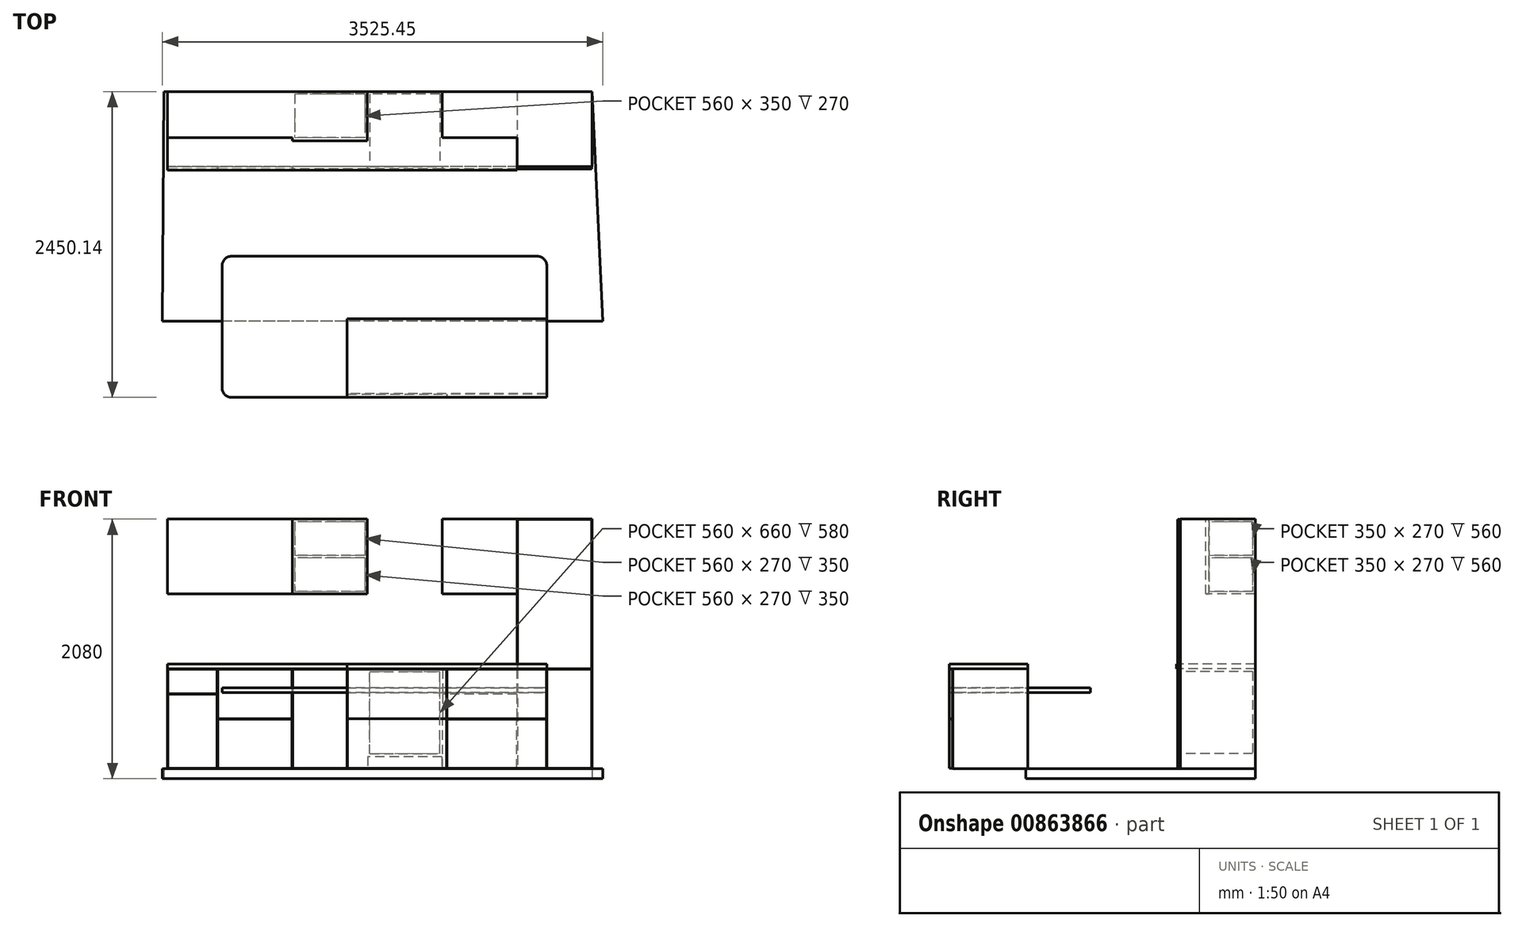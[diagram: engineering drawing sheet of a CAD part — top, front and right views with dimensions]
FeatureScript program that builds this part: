
annotation { "Feature Type Name" : "Feature", "Feature Type Description" : "" }
export const myFeature = defineFeature(function(context is Context, id is Id, definition is map)
    precondition{}
    {
        {
            var Q0;
            Q0=qCreatedBy(makeId("Top.planeOp"),FACE);
            var sketch = newSketch(context, id + "F0", { "sketchPlane" : qUnion([Q0])});
            skLineSegment(sketch, "E0", {"start": v(1715.97, -225.48) * mm, "end": v(-1714.03, -225.48) * mm});
            skLineSegment(sketch, "E1", {"start": v(1800.72, -2063.55) * mm, "end": v(1715.97, -225.48) * mm});
            skLineSegment(sketch, "E2", {"start": v(1800.72, -2063.55) * mm, "end": v(-1724.73, -2063.55) * mm});
            skLineSegment(sketch, "E3", {"start": v(-1714.03, -225.48) * mm, "end": v(-1724.73, -2063.55) * mm});
            skSolve(sketch);
        }
        {
            var Q0;
            Q0=makeQuery(id+"F0.imprint","IMPRINT",FACE,{"disambiguationData":[TD([[makeQuery(id+"F0.imprint","IMPRINT",EDGE,{"derivedFrom":sQuery(id+"F0.wireOp",EDGE,"E0")}),1.0]])]});
            var sketch = newSketch(context, id + "F1", { "sketchPlane" : qUnion([Q0])});
            skLineSegment(sketch, "E4.bottom", {"start": v(1715.97, -225.48) * mm, "end": v(1115.97, -225.48) * mm});
            skLineSegment(sketch, "E4.top", {"start": v(1715.97, -795.48) * mm, "end": v(1115.97, -795.48) * mm});
            skLineSegment(sketch, "E4.left", {"start": v(1715.97, -225.48) * mm, "end": v(1715.97, -795.48) * mm});
            skLineSegment(sketch, "E4.right", {"start": v(1115.97, -225.48) * mm, "end": v(1115.97, -795.48) * mm});
            skSolve(sketch);
        }
        {
            var Q0;
            Q0=makeQuery(id+"F1.imprint","IMPRINT",FACE,{"disambiguationData":[TD([[makeQuery(id+"F1.imprint","IMPRINT",EDGE,{"derivedFrom":sQuery(id+"F1.wireOp",EDGE,"E4.top")}),1.0]])]});
            var sketch = newSketch(context, id + "F2", { "sketchPlane" : qUnion([Q0])});
            skLineSegment(sketch, "E5.bottom", {"start": v(1115.97, -225.48) * mm, "end": v(515.97, -225.48) * mm});
            skLineSegment(sketch, "E5.top", {"start": v(1115.97, -795.48) * mm, "end": v(515.97, -795.48) * mm});
            skLineSegment(sketch, "E5.left", {"start": v(1115.97, -225.48) * mm, "end": v(1115.97, -795.48) * mm});
            skLineSegment(sketch, "E5.right", {"start": v(515.97, -225.48) * mm, "end": v(515.97, -795.48) * mm});
            skSolve(sketch);
        }
        {
            var Q0;
            Q0=makeQuery(id+"F1.imprint","IMPRINT",FACE,{"disambiguationData":[TD([[makeQuery(id+"F1.imprint","IMPRINT",EDGE,{"derivedFrom":sQuery(id+"F1.wireOp",EDGE,"E4.top")}),1.0]])]});
            var sketch = newSketch(context, id + "F3", { "sketchPlane" : qUnion([Q0])});
            skLineSegment(sketch, "E6.bottom", {"start": v(515.97, -225.48) * mm, "end": v(-84.03, -225.48) * mm});
            skLineSegment(sketch, "E6.top", {"start": v(515.97, -795.48) * mm, "end": v(-84.03, -795.48) * mm});
            skLineSegment(sketch, "E6.left", {"start": v(515.97, -225.48) * mm, "end": v(515.97, -795.48) * mm});
            skLineSegment(sketch, "E6.right", {"start": v(-84.03, -225.48) * mm, "end": v(-84.03, -795.48) * mm});
            skSolve(sketch);
        }
        {
            var Q0;
            Q0=makeQuery(id+"F3.imprint","IMPRINT",FACE,{"disambiguationData":[TD([[makeQuery(id+"F3.imprint","IMPRINT",EDGE,{"derivedFrom":sQuery(id+"F3.wireOp",EDGE,"E6.top")}),1.0]])]});
            var sketch = newSketch(context, id + "F4", { "sketchPlane" : qUnion([Q0])});
            skLineSegment(sketch, "E7.bottom", {"start": v(-84.03, -225.48) * mm, "end": v(-684.03, -225.48) * mm});
            skLineSegment(sketch, "E7.top", {"start": v(-84.03, -795.48) * mm, "end": v(-684.03, -795.48) * mm});
            skLineSegment(sketch, "E7.left", {"start": v(-84.03, -225.48) * mm, "end": v(-84.03, -795.48) * mm});
            skLineSegment(sketch, "E7.right", {"start": v(-684.03, -225.48) * mm, "end": v(-684.03, -795.48) * mm});
            skSolve(sketch);
        }
        {
            var Q0;
            Q0=makeQuery(id+"F4.imprint","IMPRINT",FACE,{"disambiguationData":[TD([[makeQuery(id+"F4.imprint","IMPRINT",EDGE,{"derivedFrom":sQuery(id+"F4.wireOp",EDGE,"E7.top")}),1.0]])]});
            var sketch = newSketch(context, id + "F5", { "sketchPlane" : qUnion([Q0])});
            skLineSegment(sketch, "E8.bottom", {"start": v(-684.03, -225.48) * mm, "end": v(-1284.03, -225.48) * mm});
            skLineSegment(sketch, "E8.top", {"start": v(-684.03, -795.48) * mm, "end": v(-1284.03, -795.48) * mm});
            skLineSegment(sketch, "E8.left", {"start": v(-684.03, -225.48) * mm, "end": v(-684.03, -795.48) * mm});
            skLineSegment(sketch, "E8.right", {"start": v(-1284.03, -225.48) * mm, "end": v(-1284.03, -795.48) * mm});
            skSolve(sketch);
        }
        {
            var Q0;
            Q0=makeQuery(id+"F1.imprint","IMPRINT",FACE,{"disambiguationData":[TD([[makeQuery(id+"F1.imprint","IMPRINT",EDGE,{"derivedFrom":sQuery(id+"F1.wireOp",EDGE,"E4.bottom")}),1.0]])]});
            cPlane(context, id + "F6", {"entities" : qUnion([Q0]), "cplaneType" : CPlaneType.OFFSET, "offset" : 80 * mm, "width" : 150 * mm, "height" : 150 * mm});
        }
        {
            var Q0;
            Q0=qCreatedBy(id+"F6.planeOp",FACE);
            var sketch = newSketch(context, id + "F7", { "sketchPlane" : qUnion([Q0])});
            skLineSegment(sketch, "E9.bottom", {"start": v(1715.97, -225.48) * mm, "end": v(1115.97, -225.48) * mm});
            skLineSegment(sketch, "E9.top", {"start": v(1715.97, -825.48) * mm, "end": v(1115.97, -825.48) * mm});
            skLineSegment(sketch, "E9.left", {"start": v(1715.97, -225.48) * mm, "end": v(1715.97, -825.48) * mm});
            skLineSegment(sketch, "E9.right", {"start": v(1115.97, -225.48) * mm, "end": v(1115.97, -825.48) * mm});
            skSolve(sketch);
        }
        {
            var Q0;
            Q0=qCreatedBy(id+"F6.planeOp",FACE);
            var sketch = newSketch(context, id + "F8", { "sketchPlane" : qUnion([Q0])});
            skLineSegment(sketch, "E10.bottom", {"start": v(1115.97, -225.48) * mm, "end": v(515.97, -225.48) * mm});
            skLineSegment(sketch, "E10.top", {"start": v(1115.97, -825.48) * mm, "end": v(515.97, -825.48) * mm});
            skLineSegment(sketch, "E10.left", {"start": v(1115.97, -225.48) * mm, "end": v(1115.97, -825.48) * mm});
            skLineSegment(sketch, "E10.right", {"start": v(515.97, -225.48) * mm, "end": v(515.97, -825.48) * mm});
            skSolve(sketch);
        }
        {
            var Q0;
            Q0=qCreatedBy(id+"F6.planeOp",FACE);
            var sketch = newSketch(context, id + "F9", { "sketchPlane" : qUnion([Q0])});
            skLineSegment(sketch, "E11.bottom", {"start": v(515.97, -225.48) * mm, "end": v(-84.03, -225.48) * mm});
            skLineSegment(sketch, "E11.top", {"start": v(515.97, -825.48) * mm, "end": v(-84.03, -825.48) * mm});
            skLineSegment(sketch, "E11.left", {"start": v(515.97, -225.48) * mm, "end": v(515.97, -825.48) * mm});
            skLineSegment(sketch, "E11.right", {"start": v(-84.03, -225.48) * mm, "end": v(-84.03, -825.48) * mm});
            skSolve(sketch);
        }
        {
            var Q0;
            Q0=qCreatedBy(id+"F6.planeOp",FACE);
            var sketch = newSketch(context, id + "F10", { "sketchPlane" : qUnion([Q0])});
            skLineSegment(sketch, "E12.bottom", {"start": v(-84.03, -225.48) * mm, "end": v(-684.03, -225.48) * mm});
            skLineSegment(sketch, "E12.top", {"start": v(-84.03, -825.48) * mm, "end": v(-684.03, -825.48) * mm});
            skLineSegment(sketch, "E12.left", {"start": v(-84.03, -225.48) * mm, "end": v(-84.03, -825.48) * mm});
            skLineSegment(sketch, "E12.right", {"start": v(-684.03, -225.48) * mm, "end": v(-684.03, -825.48) * mm});
            skSolve(sketch);
        }
        {
            var Q0;
            Q0=qCreatedBy(id+"F6.planeOp",FACE);
            var sketch = newSketch(context, id + "F11", { "sketchPlane" : qUnion([Q0])});
            skLineSegment(sketch, "E13.bottom", {"start": v(-684.03, -225.48) * mm, "end": v(-1284.03, -225.48) * mm});
            skLineSegment(sketch, "E13.top", {"start": v(-684.03, -825.48) * mm, "end": v(-1284.03, -825.48) * mm});
            skLineSegment(sketch, "E13.left", {"start": v(-684.03, -225.48) * mm, "end": v(-684.03, -825.48) * mm});
            skLineSegment(sketch, "E13.right", {"start": v(-1284.03, -225.48) * mm, "end": v(-1284.03, -825.48) * mm});
            skSolve(sketch);
        }
        {
            var Q0;
            Q0=qCreatedBy(id+"F6.planeOp",FACE);
            var sketch = newSketch(context, id + "F12", { "sketchPlane" : qUnion([Q0])});
            skLineSegment(sketch, "E14.bottom", {"start": v(-1284.03, -225.48) * mm, "end": v(-1684.03, -225.48) * mm});
            skLineSegment(sketch, "E14.top", {"start": v(-1284.03, -825.48) * mm, "end": v(-1684.03, -825.48) * mm});
            skLineSegment(sketch, "E14.left", {"start": v(-1284.03, -225.48) * mm, "end": v(-1284.03, -825.48) * mm});
            skLineSegment(sketch, "E14.right", {"start": v(-1684.03, -225.48) * mm, "end": v(-1684.03, -825.48) * mm});
            skSolve(sketch);
        }
        {
            var Q0;
            Q0=makeQuery(id+"F7.imprint","IMPRINT",FACE,{"disambiguationData":[TD([[makeQuery(id+"F7.imprint","IMPRINT",EDGE,{"derivedFrom":sQuery(id+"F7.wireOp",EDGE,"E9.bottom")}),1.0]])]});
            extrude(context, id + "F13", {"entities" : qUnion([Q0]), "depth" : 2000 * mm, "offsetDistance" : 25 * mm});
        }
        {
            var Q0;
            Q0=makeQuery(id+"F8.imprint","IMPRINT",FACE,{"disambiguationData":[TD([[makeQuery(id+"F8.imprint","IMPRINT",EDGE,{"derivedFrom":sQuery(id+"F8.wireOp",EDGE,"E10.bottom")}),1.0]])]});
            extrude(context, id + "F14", {"entities" : qUnion([Q0]), "operationType" : NewBodyOperationType.ADD, "depth" : 800 * mm, "offsetDistance" : 25 * mm});
        }
        {
            var Q0;
            Q0=makeQuery(id+"F9.imprint","IMPRINT",FACE,{"disambiguationData":[TD([[makeQuery(id+"F9.imprint","IMPRINT",EDGE,{"derivedFrom":sQuery(id+"F9.wireOp",EDGE,"E11.bottom")}),1.0]])]});
            extrude(context, id + "F15", {"entities" : qUnion([Q0]), "operationType" : NewBodyOperationType.ADD, "depth" : 800 * mm, "offsetDistance" : 25 * mm});
        }
        {
            var Q0;
            Q0=makeQuery(id+"F10.imprint","IMPRINT",FACE,{"disambiguationData":[TD([[makeQuery(id+"F10.imprint","IMPRINT",EDGE,{"derivedFrom":sQuery(id+"F10.wireOp",EDGE,"E12.bottom")}),1.0]])]});
            extrude(context, id + "F16", {"entities" : qUnion([Q0]), "operationType" : NewBodyOperationType.ADD, "depth" : 800 * mm, "offsetDistance" : 25 * mm});
        }
        {
            var Q0;
            Q0=makeQuery(id+"F11.imprint","IMPRINT",FACE,{"disambiguationData":[TD([[makeQuery(id+"F11.imprint","IMPRINT",EDGE,{"derivedFrom":sQuery(id+"F11.wireOp",EDGE,"E13.bottom")}),1.0]])]});
            extrude(context, id + "F17", {"entities" : qUnion([Q0]), "operationType" : NewBodyOperationType.ADD, "depth" : 800 * mm, "offsetDistance" : 25 * mm});
        }
        {
            var Q0;
            Q0=makeQuery(id+"F12.imprint","IMPRINT",FACE,{"disambiguationData":[TD([[makeQuery(id+"F12.imprint","IMPRINT",EDGE,{"derivedFrom":sQuery(id+"F12.wireOp",EDGE,"E14.bottom")}),1.0]])]});
            extrude(context, id + "F18", {"entities" : qUnion([Q0]), "operationType" : NewBodyOperationType.ADD, "depth" : 800 * mm, "offsetDistance" : 25 * mm});
        }
        {
            var Q0;
            Q0=makeQuery(id+"F13.opExtrude","CAP_FACE",FACE,{"disambiguationData":[OSD([sQuery(id+"F7.wireOp",EDGE,"E9.bottom"),sQuery(id+"F7.wireOp",EDGE,"E9.top"),sQuery(id+"F7.wireOp",EDGE,"E9.left"),sQuery(id+"F7.wireOp",EDGE,"E9.right")])],"isStart":false});
            var sketch = newSketch(context, id + "F19", { "sketchPlane" : qUnion([Q0])});
            skLineSegment(sketch, "E15.bottom", {"start": v(1115.97, -225.48) * mm, "end": v(515.97, -225.48) * mm});
            skLineSegment(sketch, "E15.top", {"start": v(1115.97, -595.48) * mm, "end": v(515.97, -595.48) * mm});
            skLineSegment(sketch, "E15.left", {"start": v(1115.97, -225.48) * mm, "end": v(1115.97, -595.48) * mm});
            skLineSegment(sketch, "E15.right", {"start": v(515.97, -225.48) * mm, "end": v(515.97, -595.48) * mm});
            skSolve(sketch);
        }
        {
            var Q0;
            Q0=makeQuery(id+"F19.imprint","IMPRINT",FACE,{"disambiguationData":[TD([[makeQuery(id+"F19.imprint","IMPRINT",EDGE,{"derivedFrom":sQuery(id+"F19.wireOp",EDGE,"E15.bottom")}),1.0]])]});
            var sketch = newSketch(context, id + "F20", { "sketchPlane" : qUnion([Q0])});
            skLineSegment(sketch, "E16.bottom", {"start": v(515.97, -225.48) * mm, "end": v(-84.03, -225.48) * mm});
            skLineSegment(sketch, "E16.top", {"start": v(515.97, -595.48) * mm, "end": v(-84.03, -595.48) * mm});
            skLineSegment(sketch, "E16.left", {"start": v(515.97, -225.48) * mm, "end": v(515.97, -595.48) * mm});
            skLineSegment(sketch, "E16.right", {"start": v(-84.03, -225.48) * mm, "end": v(-84.03, -595.48) * mm});
            skSolve(sketch);
        }
        {
            var Q0;
            Q0=makeQuery(id+"F20.imprint","IMPRINT",FACE,{"disambiguationData":[TD([[makeQuery(id+"F20.imprint","IMPRINT",EDGE,{"derivedFrom":sQuery(id+"F20.wireOp",EDGE,"E16.bottom")}),1.0]])]});
            var sketch = newSketch(context, id + "F21", { "sketchPlane" : qUnion([Q0])});
            skLineSegment(sketch, "E17.bottom", {"start": v(-84.03, -225.48) * mm, "end": v(-684.03, -225.48) * mm});
            skLineSegment(sketch, "E17.top", {"start": v(-84.03, -595.48) * mm, "end": v(-684.03, -595.48) * mm});
            skLineSegment(sketch, "E17.left", {"start": v(-84.03, -225.48) * mm, "end": v(-84.03, -595.48) * mm});
            skLineSegment(sketch, "E17.right", {"start": v(-684.03, -225.48) * mm, "end": v(-684.03, -595.48) * mm});
            skSolve(sketch);
        }
        {
            var Q0;
            Q0=makeQuery(id+"F21.imprint","IMPRINT",FACE,{"disambiguationData":[TD([[makeQuery(id+"F21.imprint","IMPRINT",EDGE,{"derivedFrom":sQuery(id+"F21.wireOp",EDGE,"E17.bottom")}),1.0]])]});
            var sketch = newSketch(context, id + "F22", { "sketchPlane" : qUnion([Q0])});
            skLineSegment(sketch, "E18.bottom", {"start": v(-684.03, -225.48) * mm, "end": v(-1284.03, -225.48) * mm});
            skLineSegment(sketch, "E18.top", {"start": v(-684.03, -595.48) * mm, "end": v(-1284.03, -595.48) * mm});
            skLineSegment(sketch, "E18.left", {"start": v(-684.03, -225.48) * mm, "end": v(-684.03, -595.48) * mm});
            skLineSegment(sketch, "E18.right", {"start": v(-1284.03, -225.48) * mm, "end": v(-1284.03, -595.48) * mm});
            skSolve(sketch);
        }
        {
            var Q0;
            Q0=makeQuery(id+"F18.boolean.opBoolean","MERGE",FACE,{"derivedFrom":[makeQuery(id+"F17.boolean.opBoolean","MERGE",FACE,{"derivedFrom":[makeQuery(id+"F16.boolean.opBoolean","MERGE",FACE,{"derivedFrom":[makeQuery(id+"F15.boolean.opBoolean","MERGE",FACE,{"derivedFrom":[makeQuery(id+"F14.opExtrude","CAP_FACE",FACE,{"disambiguationData":[OSD([sQuery(id+"F8.wireOp",EDGE,"E10.bottom"),sQuery(id+"F8.wireOp",EDGE,"E10.top"),sQuery(id+"F8.wireOp",EDGE,"E10.left"),sQuery(id+"F8.wireOp",EDGE,"E10.right")])],"isStart":false}),makeQuery(id+"F15.opExtrude","CAP_FACE",FACE,{"disambiguationData":[OSD([sQuery(id+"F9.wireOp",EDGE,"E11.bottom"),sQuery(id+"F9.wireOp",EDGE,"E11.top"),sQuery(id+"F9.wireOp",EDGE,"E11.left"),sQuery(id+"F9.wireOp",EDGE,"E11.right")])],"isStart":false})]}),makeQuery(id+"F16.opExtrude","CAP_FACE",FACE,{"disambiguationData":[OSD([sQuery(id+"F10.wireOp",EDGE,"E12.bottom"),sQuery(id+"F10.wireOp",EDGE,"E12.top"),sQuery(id+"F10.wireOp",EDGE,"E12.left"),sQuery(id+"F10.wireOp",EDGE,"E12.right")])],"isStart":false})]}),makeQuery(id+"F17.opExtrude","CAP_FACE",FACE,{"disambiguationData":[OSD([sQuery(id+"F11.wireOp",EDGE,"E13.bottom"),sQuery(id+"F11.wireOp",EDGE,"E13.top"),sQuery(id+"F11.wireOp",EDGE,"E13.left"),sQuery(id+"F11.wireOp",EDGE,"E13.right")])],"isStart":false})]}),makeQuery(id+"F18.opExtrude","CAP_FACE",FACE,{"disambiguationData":[OSD([sQuery(id+"F12.wireOp",EDGE,"E14.bottom"),sQuery(id+"F12.wireOp",EDGE,"E14.top"),sQuery(id+"F12.wireOp",EDGE,"E14.left"),sQuery(id+"F12.wireOp",EDGE,"E14.right")])],"isStart":false})]});
            var sketch = newSketch(context, id + "F23", { "sketchPlane" : qUnion([Q0])});
            skLineSegment(sketch, "E19.bottom", {"start": v(-1284.03, -225.48) * mm, "end": v(-1684.03, -225.48) * mm});
            skLineSegment(sketch, "E19.top", {"start": v(-1284.03, -595.48) * mm, "end": v(-1684.03, -595.48) * mm});
            skLineSegment(sketch, "E19.left", {"start": v(-1284.03, -225.48) * mm, "end": v(-1284.03, -595.48) * mm});
            skLineSegment(sketch, "E19.right", {"start": v(-1684.03, -225.48) * mm, "end": v(-1684.03, -595.48) * mm});
            skSolve(sketch);
        }
        {
            var Q0;
            Q0 = qSketchRegion(id + "F23", true);
            extrude(context, id + "F24", {"entities" : qUnion([Q0]), "operationType" : NewBodyOperationType.ADD, "depth" : 1200 * mm, "offsetDistance" : 25 * mm});
        }
        {
            var Q0;
            Q0=makeQuery(id+"F24.opExtrude","SWEPT_FACE",FACE,{"disambiguationData":[OSD([sQuery(id+"F23.wireOp",EDGE,"E19.top")])]});
            var sketch = newSketch(context, id + "F25", { "sketchPlane" : qUnion([Q0])});
            skLineSegment(sketch, "E20.bottom", {"start": v(-1684.03, 880) * mm, "end": v(-1284.03, 880) * mm});
            skLineSegment(sketch, "E20.top", {"start": v(-1684.03, 1480) * mm, "end": v(-1284.03, 1480) * mm});
            skLineSegment(sketch, "E20.left", {"start": v(-1684.03, 880) * mm, "end": v(-1684.03, 1480) * mm});
            skLineSegment(sketch, "E20.right", {"start": v(-1284.03, 880) * mm, "end": v(-1284.03, 1480) * mm});
            skSolve(sketch);
        }
        {
            var Q0;
            Q0 = qSketchRegion(id + "F25", true);
            extrude(context, id + "F26", {"entities" : qUnion([Q0]), "operationType" : NewBodyOperationType.REMOVE, "oppositeDirection" : true, "depth" : 370 * mm, "offsetDistance" : 25 * mm});
        }
        {
            var Q0;
            Q0=makeQuery(id+"F22.imprint","IMPRINT",FACE,{"disambiguationData":[TD([[makeQuery(id+"F22.imprint","IMPRINT",EDGE,{"derivedFrom":sQuery(id+"F22.wireOp",EDGE,"E18.bottom")}),1.0]])]});
            extrude(context, id + "F27", {"entities" : qUnion([Q0]), "operationType" : NewBodyOperationType.ADD, "oppositeDirection" : true, "depth" : 600 * mm, "offsetDistance" : 25 * mm});
        }
        {
            var Q0;
            Q0=makeQuery(id+"F21.imprint","IMPRINT",FACE,{"disambiguationData":[TD([[makeQuery(id+"F21.imprint","IMPRINT",EDGE,{"derivedFrom":sQuery(id+"F21.wireOp",EDGE,"E17.bottom")}),1.0]])]});
            extrude(context, id + "F28", {"entities" : qUnion([Q0]), "operationType" : NewBodyOperationType.ADD, "oppositeDirection" : true, "depth" : 600 * mm, "offsetDistance" : 25 * mm});
        }
        {
            var Q0;
            Q0=makeQuery(id+"F20.imprint","IMPRINT",FACE,{"disambiguationData":[TD([[makeQuery(id+"F20.imprint","IMPRINT",EDGE,{"derivedFrom":sQuery(id+"F20.wireOp",EDGE,"E16.left")}),1.0]])]});
            extrude(context, id + "F29", {"entities" : qUnion([Q0]), "operationType" : NewBodyOperationType.ADD, "oppositeDirection" : true, "depth" : 600 * mm, "offsetDistance" : 25 * mm});
        }
        {
            var Q0;
            Q0=makeQuery(id+"F18.boolean.opBoolean","MERGE",FACE,{"derivedFrom":[makeQuery(id+"F17.boolean.opBoolean","MERGE",FACE,{"derivedFrom":[makeQuery(id+"F16.boolean.opBoolean","MERGE",FACE,{"derivedFrom":[makeQuery(id+"F15.boolean.opBoolean","MERGE",FACE,{"derivedFrom":[makeQuery(id+"F14.boolean.opBoolean","MERGE",FACE,{"derivedFrom":[makeQuery(id+"F13.opExtrude","SWEPT_FACE",FACE,{"disambiguationData":[OSD([sQuery(id+"F7.wireOp",EDGE,"E9.top")])]}),makeQuery(id+"F14.opExtrude","SWEPT_FACE",FACE,{"disambiguationData":[OSD([sQuery(id+"F8.wireOp",EDGE,"E10.top")])]})]}),makeQuery(id+"F15.opExtrude","SWEPT_FACE",FACE,{"disambiguationData":[OSD([sQuery(id+"F9.wireOp",EDGE,"E11.top")])]})]}),makeQuery(id+"F16.opExtrude","SWEPT_FACE",FACE,{"disambiguationData":[OSD([sQuery(id+"F10.wireOp",EDGE,"E12.top")])]})]}),makeQuery(id+"F17.opExtrude","SWEPT_FACE",FACE,{"disambiguationData":[OSD([sQuery(id+"F11.wireOp",EDGE,"E13.top")])]})]}),makeQuery(id+"F18.opExtrude","SWEPT_FACE",FACE,{"disambiguationData":[OSD([sQuery(id+"F12.wireOp",EDGE,"E14.top")])]})]});
            extrude(context, id + "F30", {"entities" : qUnion([Q0]), "depth" : 20 * mm, "offsetDistance" : 25 * mm});
        }
        {
            var Q0;
            Q0=makeQuery(id+"F30.opExtrude","CAP_FACE",FACE,{"disambiguationData":[OSD([sQuery(id+"F7.wireOp",EDGE,"E9.top"),sQuery(id+"F8.wireOp",EDGE,"E10.top"),sQuery(id+"F9.wireOp",EDGE,"E11.top"),sQuery(id+"F10.wireOp",EDGE,"E12.top"),sQuery(id+"F11.wireOp",EDGE,"E13.top"),sQuery(id+"F12.wireOp",EDGE,"E14.top")])],"isStart":false});
            var sketch = newSketch(context, id + "F31", { "sketchPlane" : qUnion([Q0])});
            skLineSegment(sketch, "E21.bottom", {"start": v(1715.97, 2080) * mm, "end": v(1115.97, 2080) * mm});
            skLineSegment(sketch, "E21.top", {"start": v(1715.97, 880) * mm, "end": v(1115.97, 880) * mm});
            skLineSegment(sketch, "E21.left", {"start": v(1715.97, 2080) * mm, "end": v(1715.97, 880) * mm});
            skLineSegment(sketch, "E21.right", {"start": v(1115.97, 2080) * mm, "end": v(1115.97, 880) * mm});
            skLineSegment(sketch, "E22.top", {"start": v(1715.97, 80) * mm, "end": v(1115.97, 80) * mm});
            skLineSegment(sketch, "E22.left", {"start": v(1715.97, 880) * mm, "end": v(1715.97, 80) * mm});
            skLineSegment(sketch, "E22.right", {"start": v(1115.97, 880) * mm, "end": v(1115.97, 80) * mm});
            skLineSegment(sketch, "E23.0", {"start": v(1713.47, 2077.5) * mm, "end": v(1713.47, 880) * mm});
            skLineSegment(sketch, "E23.1", {"start": v(1713.47, 2077.5) * mm, "end": v(1118.47, 2077.5) * mm});
            skLineSegment(sketch, "E23.2", {"start": v(1118.47, 2077.5) * mm, "end": v(1118.47, 880) * mm});
            skLineSegment(sketch, "E24.0", {"start": v(1118.47, 877.5) * mm, "end": v(1118.47, 82.5) * mm});
            skLineSegment(sketch, "E24.1", {"start": v(1713.47, 877.5) * mm, "end": v(1118.47, 877.5) * mm});
            skLineSegment(sketch, "E24.2", {"start": v(1713.47, 877.5) * mm, "end": v(1713.47, 82.5) * mm});
            skLineSegment(sketch, "E24.3", {"start": v(1713.47, 82.5) * mm, "end": v(1118.47, 82.5) * mm});
            skSolve(sketch);
        }
        {
            var Q0;
            Q0=makeQuery(id+"F31.imprint","IMPRINT",FACE,{"disambiguationData":[TD([[makeQuery(id+"F31.imprint","IMPRINT",EDGE,{"derivedFrom":sQuery(id+"F31.wireOp",EDGE,"E21.bottom")}),1.0]])]});
            extrude(context, id + "F32", {"entities" : qUnion([Q0]), "operationType" : NewBodyOperationType.REMOVE, "oppositeDirection" : true, "depth" : 20 * mm, "offsetDistance" : 25 * mm});
        }
        {
            var Q0;
            Q0=makeQuery(id+"F31.imprint","IMPRINT",FACE,{"disambiguationData":[TD([[makeQuery(id+"F31.imprint","IMPRINT",EDGE,{"derivedFrom":sQuery(id+"F31.wireOp",EDGE,"E22.top")}),-1.0]])]});
            extrude(context, id + "F33", {"entities" : qUnion([Q0]), "operationType" : NewBodyOperationType.REMOVE, "oppositeDirection" : true, "depth" : 20 * mm, "offsetDistance" : 25 * mm});
        }
        {
            var Q0;
            {var subQ0=sQuery(id+"F12.wireOp",EDGE,"E14.top");var subQ1=sQuery(id+"F11.wireOp",EDGE,"E13.top");var subQ2=sQuery(id+"F10.wireOp",EDGE,"E12.top");var subQ3=sQuery(id+"F9.wireOp",EDGE,"E11.top");var subQ4=sQuery(id+"F8.wireOp",EDGE,"E10.top");var subQ5=sQuery(id+"F7.wireOp",EDGE,"E9.top");Q0=makeQuery(id+"F33.boolean.opBoolean","SPLIT",FACE,{"disambiguationData":[TD([makeQuery(id+"F33.opExtrude","SWEPT_FACE",FACE,{"disambiguationData":[OSD([sQuery(id+"F31.wireOp",EDGE,"E22.right")])]})])],"derivedFrom":makeQuery(id+"F30.opExtrude","CAP_FACE",FACE,{"disambiguationData":[OSD([subQ5,subQ4,subQ3,subQ2,subQ1,subQ0])],"isStart":false})});}
            var sketch = newSketch(context, id + "F34", { "sketchPlane" : qUnion([Q0])});
            skLineSegment(sketch, "E25.bottom", {"start": v(-1684.03, 880) * mm, "end": v(-1284.03, 880) * mm});
            skLineSegment(sketch, "E25.top", {"start": v(-1684.03, 680) * mm, "end": v(-1284.03, 680) * mm});
            skLineSegment(sketch, "E25.left", {"start": v(-1684.03, 880) * mm, "end": v(-1684.03, 680) * mm});
            skLineSegment(sketch, "E25.right", {"start": v(-1284.03, 880) * mm, "end": v(-1284.03, 680) * mm});
            skLineSegment(sketch, "E26.top", {"start": v(-1684.03, 80) * mm, "end": v(-1284.03, 80) * mm});
            skLineSegment(sketch, "E26.left", {"start": v(-1684.03, 680) * mm, "end": v(-1684.03, 80) * mm});
            skLineSegment(sketch, "E26.right", {"start": v(-1284.03, 680) * mm, "end": v(-1284.03, 80) * mm});
            skLineSegment(sketch, "E27.0", {"start": v(-1286.53, 877.5) * mm, "end": v(-1286.53, 680) * mm});
            skLineSegment(sketch, "E27.1", {"start": v(-1681.53, 877.5) * mm, "end": v(-1286.53, 877.5) * mm});
            skLineSegment(sketch, "E27.2", {"start": v(-1681.53, 877.5) * mm, "end": v(-1681.53, 680) * mm});
            skLineSegment(sketch, "E28.0", {"start": v(-1681.53, 677.5) * mm, "end": v(-1681.53, 82.5) * mm});
            skLineSegment(sketch, "E28.1", {"start": v(-1681.53, 677.5) * mm, "end": v(-1286.53, 677.5) * mm});
            skLineSegment(sketch, "E28.2", {"start": v(-1286.53, 677.5) * mm, "end": v(-1286.53, 82.5) * mm});
            skLineSegment(sketch, "E28.3", {"start": v(-1681.53, 82.5) * mm, "end": v(-1286.53, 82.5) * mm});
            skSolve(sketch);
        }
        {
            var Q0;
            Q0=makeQuery(id+"F34.imprint","IMPRINT",FACE,{"disambiguationData":[TD([[makeQuery(id+"F34.imprint","IMPRINT",EDGE,{"derivedFrom":sQuery(id+"F34.wireOp",EDGE,"E25.bottom")}),1.0]])]});
            extrude(context, id + "F35", {"entities" : qUnion([Q0]), "operationType" : NewBodyOperationType.REMOVE, "oppositeDirection" : true, "depth" : 20 * mm, "offsetDistance" : 25 * mm});
        }
        {
            var Q0;
            Q0=makeQuery(id+"F34.imprint","IMPRINT",FACE,{"disambiguationData":[TD([[makeQuery(id+"F34.imprint","IMPRINT",EDGE,{"derivedFrom":sQuery(id+"F34.wireOp",EDGE,"E26.top")}),-1.0]])]});
            extrude(context, id + "F36", {"entities" : qUnion([Q0]), "operationType" : NewBodyOperationType.REMOVE, "oppositeDirection" : true, "depth" : 20 * mm, "offsetDistance" : 25 * mm});
        }
        {
            var Q0;
            {var subQ0=makeQuery(id+"F33.opExtrude","SWEPT_FACE",FACE,{"disambiguationData":[OSD([sQuery(id+"F31.wireOp",EDGE,"E22.right")])]});var subQ1=sQuery(id+"F12.wireOp",EDGE,"E14.top");var subQ2=sQuery(id+"F11.wireOp",EDGE,"E13.top");var subQ3=sQuery(id+"F10.wireOp",EDGE,"E12.top");var subQ4=sQuery(id+"F9.wireOp",EDGE,"E11.top");var subQ5=sQuery(id+"F8.wireOp",EDGE,"E10.top");var subQ6=sQuery(id+"F7.wireOp",EDGE,"E9.top");Q0=makeQuery(id+"F36.boolean.opBoolean","SPLIT",FACE,{"disambiguationData":[TD([makeQuery(id+"F33.boolean.opBoolean","COPY",FACE,{"derivedFrom":subQ0})])],"derivedFrom":makeQuery(id+"F33.boolean.opBoolean","SPLIT",FACE,{"disambiguationData":[TD([subQ0])],"derivedFrom":makeQuery(id+"F30.opExtrude","CAP_FACE",FACE,{"disambiguationData":[OSD([subQ6,subQ5,subQ4,subQ3,subQ2,subQ1])],"isStart":false})})});}
            var sketch = newSketch(context, id + "F37", { "sketchPlane" : qUnion([Q0])});
            skLineSegment(sketch, "E29.bottom", {"start": v(-1284.03, 880) * mm, "end": v(-684.03, 880) * mm});
            skLineSegment(sketch, "E29.top", {"start": v(-1284.03, 480) * mm, "end": v(-684.03, 480) * mm});
            skLineSegment(sketch, "E29.left", {"start": v(-1284.03, 880) * mm, "end": v(-1284.03, 480) * mm});
            skLineSegment(sketch, "E29.right", {"start": v(-684.03, 880) * mm, "end": v(-684.03, 480) * mm});
            skLineSegment(sketch, "E30.0", {"start": v(-1281.53, 877.5) * mm, "end": v(-686.53, 877.5) * mm});
            skLineSegment(sketch, "E30.1", {"start": v(-1281.53, 877.5) * mm, "end": v(-1281.53, 482.5) * mm});
            skLineSegment(sketch, "E30.2", {"start": v(-1281.53, 482.5) * mm, "end": v(-686.53, 482.5) * mm});
            skLineSegment(sketch, "E30.3", {"start": v(-686.53, 877.5) * mm, "end": v(-686.53, 482.5) * mm});
            skLineSegment(sketch, "E31.bottom", {"start": v(-1284.03, 80) * mm, "end": v(-684.03, 80) * mm});
            skLineSegment(sketch, "E31.left", {"start": v(-1284.03, 80) * mm, "end": v(-1284.03, 480) * mm});
            skLineSegment(sketch, "E31.right", {"start": v(-684.03, 80) * mm, "end": v(-684.03, 480) * mm});
            skLineSegment(sketch, "E32.0", {"start": v(-1281.53, 477.5) * mm, "end": v(-686.53, 477.5) * mm});
            skLineSegment(sketch, "E32.1", {"start": v(-1281.53, 82.5) * mm, "end": v(-1281.53, 477.5) * mm});
            skLineSegment(sketch, "E32.2", {"start": v(-1281.53, 82.5) * mm, "end": v(-686.53, 82.5) * mm});
            skLineSegment(sketch, "E32.3", {"start": v(-686.53, 82.5) * mm, "end": v(-686.53, 477.5) * mm});
            skSolve(sketch);
        }
        {
            var Q0;
            Q0=makeQuery(id+"F37.imprint","IMPRINT",FACE,{"disambiguationData":[TD([[makeQuery(id+"F37.imprint","IMPRINT",EDGE,{"derivedFrom":sQuery(id+"F37.wireOp",EDGE,"E29.bottom")}),1.0]])]});
            extrude(context, id + "F38", {"entities" : qUnion([Q0]), "operationType" : NewBodyOperationType.REMOVE, "oppositeDirection" : true, "depth" : 20 * mm, "offsetDistance" : 25 * mm});
        }
        {
            var Q0;
            Q0=makeQuery(id+"F37.imprint","IMPRINT",FACE,{"disambiguationData":[TD([[makeQuery(id+"F37.imprint","IMPRINT",EDGE,{"derivedFrom":sQuery(id+"F37.wireOp",EDGE,"E31.bottom")}),-1.0]])]});
            extrude(context, id + "F39", {"entities" : qUnion([Q0]), "operationType" : NewBodyOperationType.REMOVE, "oppositeDirection" : true, "depth" : 20 * mm, "offsetDistance" : 25 * mm});
        }
        {
            var Q0;
            {var subQ1=makeQuery(id+"F33.opExtrude","SWEPT_FACE",FACE,{"disambiguationData":[OSD([sQuery(id+"F31.wireOp",EDGE,"E22.right")])]});var subQ2=makeQuery(id+"F33.boolean.opBoolean","COPY",FACE,{"derivedFrom":subQ1});var subQ3=sQuery(id+"F12.wireOp",EDGE,"E14.top");var subQ4=sQuery(id+"F11.wireOp",EDGE,"E13.top");var subQ5=sQuery(id+"F10.wireOp",EDGE,"E12.top");var subQ6=sQuery(id+"F9.wireOp",EDGE,"E11.top");var subQ7=sQuery(id+"F8.wireOp",EDGE,"E10.top");var subQ8=sQuery(id+"F7.wireOp",EDGE,"E9.top");Q0=makeQuery(id+"F39.boolean.opBoolean","SPLIT",FACE,{"disambiguationData":[TD([subQ2])],"derivedFrom":makeQuery(id+"F38.boolean.opBoolean","SPLIT",FACE,{"disambiguationData":[TD([subQ2])],"derivedFrom":makeQuery(id+"F36.boolean.opBoolean","SPLIT",FACE,{"disambiguationData":[TD([subQ2])],"derivedFrom":makeQuery(id+"F33.boolean.opBoolean","SPLIT",FACE,{"disambiguationData":[TD([subQ1])],"derivedFrom":makeQuery(id+"F30.opExtrude","CAP_FACE",FACE,{"disambiguationData":[OSD([subQ8,subQ7,subQ6,subQ5,subQ4,subQ3])],"isStart":false})})})})});}
            var sketch = newSketch(context, id + "F40", { "sketchPlane" : qUnion([Q0])});
            skLineSegment(sketch, "E33.bottom", {"start": v(-84.03, 880) * mm, "end": v(-684.03, 880) * mm});
            skLineSegment(sketch, "E33.top", {"start": v(-84.03, 80) * mm, "end": v(-684.03, 80) * mm});
            skLineSegment(sketch, "E33.left", {"start": v(-84.03, 880) * mm, "end": v(-84.03, 80) * mm});
            skLineSegment(sketch, "E33.right", {"start": v(-684.03, 880) * mm, "end": v(-684.03, 80) * mm});
            skLineSegment(sketch, "E34.0", {"start": v(-86.53, 877.5) * mm, "end": v(-681.53, 877.5) * mm});
            skLineSegment(sketch, "E34.1", {"start": v(-86.53, 877.5) * mm, "end": v(-86.53, 82.5) * mm});
            skLineSegment(sketch, "E34.2", {"start": v(-86.53, 82.5) * mm, "end": v(-681.53, 82.5) * mm});
            skLineSegment(sketch, "E34.3", {"start": v(-681.53, 877.5) * mm, "end": v(-681.53, 82.5) * mm});
            skSolve(sketch);
        }
        {
            var Q0;
            Q0=makeQuery(id+"F40.imprint","IMPRINT",FACE,{"disambiguationData":[TD([[makeQuery(id+"F40.imprint","IMPRINT",EDGE,{"derivedFrom":sQuery(id+"F40.wireOp",EDGE,"E33.bottom")}),1.0]])]});
            extrude(context, id + "F41", {"entities" : qUnion([Q0]), "operationType" : NewBodyOperationType.REMOVE, "oppositeDirection" : true, "depth" : 20 * mm, "offsetDistance" : 25 * mm});
        }
        {
            var Q0;
            {var subQ0=sQuery(id+"F12.wireOp",EDGE,"E14.top");var subQ1=sQuery(id+"F11.wireOp",EDGE,"E13.top");var subQ2=sQuery(id+"F10.wireOp",EDGE,"E12.top");var subQ3=sQuery(id+"F9.wireOp",EDGE,"E11.top");var subQ4=sQuery(id+"F8.wireOp",EDGE,"E10.top");var subQ6=sQuery(id+"F7.wireOp",EDGE,"E9.top");var subQ8=makeQuery(id+"F33.opExtrude","SWEPT_FACE",FACE,{"disambiguationData":[OSD([sQuery(id+"F31.wireOp",EDGE,"E22.right")])]});var subQ9=makeQuery(id+"F33.boolean.opBoolean","COPY",FACE,{"derivedFrom":subQ8});Q0=makeQuery(id+"F41.boolean.opBoolean","SPLIT",FACE,{"disambiguationData":[TD([subQ9])],"derivedFrom":makeQuery(id+"F39.boolean.opBoolean","SPLIT",FACE,{"disambiguationData":[TD([subQ9])],"derivedFrom":makeQuery(id+"F38.boolean.opBoolean","SPLIT",FACE,{"disambiguationData":[TD([subQ9])],"derivedFrom":makeQuery(id+"F36.boolean.opBoolean","SPLIT",FACE,{"disambiguationData":[TD([subQ9])],"derivedFrom":makeQuery(id+"F33.boolean.opBoolean","SPLIT",FACE,{"disambiguationData":[TD([subQ8])],"derivedFrom":makeQuery(id+"F30.opExtrude","CAP_FACE",FACE,{"disambiguationData":[OSD([subQ6,subQ4,subQ3,subQ2,subQ1,subQ0])],"isStart":false})})})})})});}
            var sketch = newSketch(context, id + "F42", { "sketchPlane" : qUnion([Q0])});
            skLineSegment(sketch, "E35.bottom", {"start": v(1115.97, 80) * mm, "end": v(515.97, 80) * mm});
            skLineSegment(sketch, "E35.top", {"start": v(1115.97, 480) * mm, "end": v(515.97, 480) * mm});
            skLineSegment(sketch, "E35.left", {"start": v(1115.97, 80) * mm, "end": v(1115.97, 480) * mm});
            skLineSegment(sketch, "E35.right", {"start": v(515.97, 80) * mm, "end": v(515.97, 480) * mm});
            skLineSegment(sketch, "E36.0", {"start": v(1113.47, 477.5) * mm, "end": v(518.47, 477.5) * mm});
            skLineSegment(sketch, "E36.1", {"start": v(1113.47, 82.5) * mm, "end": v(1113.47, 477.5) * mm});
            skLineSegment(sketch, "E36.2", {"start": v(1113.47, 82.5) * mm, "end": v(518.47, 82.5) * mm});
            skLineSegment(sketch, "E36.3", {"start": v(518.47, 82.5) * mm, "end": v(518.47, 477.5) * mm});
            skSolve(sketch);
        }
        {
            var Q0;
            Q0=makeQuery(id+"F42.imprint","IMPRINT",FACE,{"disambiguationData":[TD([[makeQuery(id+"F42.imprint","IMPRINT",EDGE,{"derivedFrom":sQuery(id+"F42.wireOp",EDGE,"E35.bottom")}),-1.0]])]});
            extrude(context, id + "F43", {"entities" : qUnion([Q0]), "operationType" : NewBodyOperationType.REMOVE, "oppositeDirection" : true, "depth" : 20 * mm, "offsetDistance" : 25 * mm});
        }
        {
            var Q0;
            {var subQ1=makeQuery(id+"F33.opExtrude","SWEPT_FACE",FACE,{"disambiguationData":[OSD([sQuery(id+"F31.wireOp",EDGE,"E22.right")])]});var subQ2=makeQuery(id+"F33.boolean.opBoolean","COPY",FACE,{"derivedFrom":subQ1});var subQ3=sQuery(id+"F12.wireOp",EDGE,"E14.top");var subQ4=sQuery(id+"F11.wireOp",EDGE,"E13.top");var subQ5=sQuery(id+"F10.wireOp",EDGE,"E12.top");var subQ6=sQuery(id+"F9.wireOp",EDGE,"E11.top");var subQ7=sQuery(id+"F8.wireOp",EDGE,"E10.top");var subQ8=sQuery(id+"F7.wireOp",EDGE,"E9.top");Q0=makeQuery(id+"F43.boolean.opBoolean","SPLIT",FACE,{"disambiguationData":[TD([subQ2])],"derivedFrom":makeQuery(id+"F41.boolean.opBoolean","SPLIT",FACE,{"disambiguationData":[TD([subQ2])],"derivedFrom":makeQuery(id+"F39.boolean.opBoolean","SPLIT",FACE,{"disambiguationData":[TD([subQ2])],"derivedFrom":makeQuery(id+"F38.boolean.opBoolean","SPLIT",FACE,{"disambiguationData":[TD([subQ2])],"derivedFrom":makeQuery(id+"F36.boolean.opBoolean","SPLIT",FACE,{"disambiguationData":[TD([subQ2])],"derivedFrom":makeQuery(id+"F33.boolean.opBoolean","SPLIT",FACE,{"disambiguationData":[TD([subQ1])],"derivedFrom":makeQuery(id+"F30.opExtrude","CAP_FACE",FACE,{"disambiguationData":[OSD([subQ8,subQ7,subQ6,subQ5,subQ4,subQ3])],"isStart":false})})})})})})});}
            var sketch = newSketch(context, id + "F44", { "sketchPlane" : qUnion([Q0])});
            skLineSegment(sketch, "E37.bottom", {"start": v(1115.97, 680) * mm, "end": v(515.97, 680) * mm});
            skLineSegment(sketch, "E37.top", {"start": v(1115.97, 480) * mm, "end": v(515.97, 480) * mm});
            skLineSegment(sketch, "E37.left", {"start": v(1115.97, 680) * mm, "end": v(1115.97, 480) * mm});
            skLineSegment(sketch, "E37.right", {"start": v(515.97, 680) * mm, "end": v(515.97, 480) * mm});
            skLineSegment(sketch, "E38.0", {"start": v(1113.47, 677.5) * mm, "end": v(518.47, 677.5) * mm});
            skLineSegment(sketch, "E38.1", {"start": v(1113.47, 677.5) * mm, "end": v(1113.47, 482.5) * mm});
            skLineSegment(sketch, "E38.2", {"start": v(1113.47, 482.5) * mm, "end": v(518.47, 482.5) * mm});
            skLineSegment(sketch, "E38.3", {"start": v(518.47, 677.5) * mm, "end": v(518.47, 482.5) * mm});
            skSolve(sketch);
        }
        {
            var Q0;
            Q0=makeQuery(id+"F44.imprint","IMPRINT",FACE,{"disambiguationData":[TD([[makeQuery(id+"F44.imprint","IMPRINT",EDGE,{"derivedFrom":sQuery(id+"F44.wireOp",EDGE,"E37.bottom")}),1.0]])]});
            extrude(context, id + "F45", {"entities" : qUnion([Q0]), "operationType" : NewBodyOperationType.REMOVE, "oppositeDirection" : true, "depth" : 20 * mm, "offsetDistance" : 25 * mm});
        }
        {
            var Q0;
            {var subQ0=sQuery(id+"F31.wireOp",EDGE,"E22.right");Q0=makeQuery(id+"F31.imprint","IMPRINT",FACE,{"disambiguationData":[TD([[makeQuery(id+"F31.imprint","IMPRINT",EDGE,{"derivedFrom":subQ0}),-1.0]])]});}
            var sketch = newSketch(context, id + "F46", { "sketchPlane" : qUnion([Q0])});
            skLineSegment(sketch, "E39.bottom", {"start": v(1115.97, 880) * mm, "end": v(515.97, 880) * mm});
            skLineSegment(sketch, "E39.top", {"start": v(1115.97, 680) * mm, "end": v(515.97, 680) * mm});
            skLineSegment(sketch, "E39.left", {"start": v(1115.97, 880) * mm, "end": v(1115.97, 680) * mm});
            skLineSegment(sketch, "E39.right", {"start": v(515.97, 880) * mm, "end": v(515.97, 680) * mm});
            skLineSegment(sketch, "E40.0", {"start": v(1113.47, 877.5) * mm, "end": v(518.47, 877.5) * mm});
            skLineSegment(sketch, "E40.1", {"start": v(1113.47, 877.5) * mm, "end": v(1113.47, 682.5) * mm});
            skLineSegment(sketch, "E40.2", {"start": v(1113.47, 682.5) * mm, "end": v(518.47, 682.5) * mm});
            skLineSegment(sketch, "E40.3", {"start": v(518.47, 877.5) * mm, "end": v(518.47, 682.5) * mm});
            skSolve(sketch);
        }
        {
            var Q0;
            Q0=makeQuery(id+"F46.imprint","IMPRINT",FACE,{"disambiguationData":[TD([[makeQuery(id+"F46.imprint","IMPRINT",EDGE,{"derivedFrom":sQuery(id+"F46.wireOp",EDGE,"E39.bottom")}),1.0]])]});
            extrude(context, id + "F47", {"entities" : qUnion([Q0]), "operationType" : NewBodyOperationType.REMOVE, "oppositeDirection" : true, "depth" : 20 * mm, "offsetDistance" : 25 * mm});
        }
        {
            var Q0;
            {var subQ0=sQuery(id+"F31.wireOp",EDGE,"E22.right");Q0=makeQuery(id+"F31.imprint","IMPRINT",FACE,{"disambiguationData":[TD([[makeQuery(id+"F31.imprint","IMPRINT",EDGE,{"derivedFrom":subQ0}),-1.0]])]});}
            var sketch = newSketch(context, id + "F48", { "sketchPlane" : qUnion([Q0])});
            skLineSegment(sketch, "E41.bottom", {"start": v(515.97, 180) * mm, "end": v(-84.03, 180) * mm});
            skLineSegment(sketch, "E41.top", {"start": v(515.97, 80) * mm, "end": v(-84.03, 80) * mm});
            skLineSegment(sketch, "E41.left", {"start": v(515.97, 180) * mm, "end": v(515.97, 80) * mm});
            skLineSegment(sketch, "E41.right", {"start": v(-84.03, 180) * mm, "end": v(-84.03, 80) * mm});
            skLineSegment(sketch, "E42.0", {"start": v(513.47, 177.5) * mm, "end": v(-81.53, 177.5) * mm});
            skLineSegment(sketch, "E42.1", {"start": v(513.47, 177.5) * mm, "end": v(513.47, 82.5) * mm});
            skLineSegment(sketch, "E42.2", {"start": v(513.47, 82.5) * mm, "end": v(-81.53, 82.5) * mm});
            skLineSegment(sketch, "E42.3", {"start": v(-81.53, 177.5) * mm, "end": v(-81.53, 82.5) * mm});
            skSolve(sketch);
        }
        {
            var Q0;
            Q0=makeQuery(id+"F48.imprint","IMPRINT",FACE,{"disambiguationData":[TD([[makeQuery(id+"F48.imprint","IMPRINT",EDGE,{"derivedFrom":sQuery(id+"F48.wireOp",EDGE,"E41.bottom")}),1.0]])]});
            extrude(context, id + "F49", {"entities" : qUnion([Q0]), "operationType" : NewBodyOperationType.REMOVE, "oppositeDirection" : true, "depth" : 20 * mm, "offsetDistance" : 25 * mm});
        }
        {
            var Q0;
            {var subQ0=sQuery(id+"F31.wireOp",EDGE,"E22.right");Q0=makeQuery(id+"F31.imprint","IMPRINT",FACE,{"disambiguationData":[TD([[makeQuery(id+"F31.imprint","IMPRINT",EDGE,{"derivedFrom":subQ0}),-1.0]])]});}
            var sketch = newSketch(context, id + "F50", { "sketchPlane" : qUnion([Q0])});
            skLineSegment(sketch, "E43.bottom", {"start": v(-84.03, 180) * mm, "end": v(515.97, 180) * mm});
            skLineSegment(sketch, "E43.top", {"start": v(-84.03, 880) * mm, "end": v(515.97, 880) * mm});
            skLineSegment(sketch, "E43.left", {"start": v(-84.03, 180) * mm, "end": v(-84.03, 880) * mm});
            skLineSegment(sketch, "E43.right", {"start": v(515.97, 180) * mm, "end": v(515.97, 880) * mm});
            skLineSegment(sketch, "E44.0", {"start": v(-64.03, 860) * mm, "end": v(495.97, 860) * mm});
            skLineSegment(sketch, "E44.1", {"start": v(-64.03, 200) * mm, "end": v(-64.03, 860) * mm});
            skLineSegment(sketch, "E44.2", {"start": v(-64.03, 200) * mm, "end": v(495.97, 200) * mm});
            skLineSegment(sketch, "E44.3", {"start": v(495.97, 200) * mm, "end": v(495.97, 860) * mm});
            skSolve(sketch);
        }
        {
            var Q0;
            Q0=makeQuery(id+"F50.imprint","IMPRINT",FACE,{"disambiguationData":[TD([[makeQuery(id+"F50.imprint","IMPRINT",EDGE,{"derivedFrom":sQuery(id+"F50.wireOp",EDGE,"E43.bottom")}),1.0]])]});
            extrude(context, id + "F51", {"entities" : qUnion([Q0]), "operationType" : NewBodyOperationType.REMOVE, "oppositeDirection" : true, "depth" : 20 * mm, "offsetDistance" : 25 * mm});
        }
        {
            var Q0;
            Q0=makeQuery(id+"F50.imprint","IMPRINT",FACE,{"disambiguationData":[TD([[makeQuery(id+"F50.imprint","IMPRINT",EDGE,{"derivedFrom":sQuery(id+"F50.wireOp",EDGE,"E44.0")}),-1.0]])]});
            extrude(context, id + "F52", {"entities" : qUnion([Q0]), "operationType" : NewBodyOperationType.REMOVE, "oppositeDirection" : true, "depth" : 25 * mm, "offsetDistance" : 25 * mm});
        }
        {
            var Q0;
            Q0=makeQuery(id+"F50.imprint","IMPRINT",FACE,{"disambiguationData":[TD([[makeQuery(id+"F50.imprint","IMPRINT",EDGE,{"derivedFrom":sQuery(id+"F50.wireOp",EDGE,"E44.0")}),-1.0]])]});
            cPlane(context, id + "F53", {"entities" : qUnion([Q0]), "cplaneType" : CPlaneType.OFFSET, "offset" : 20 * mm, "oppositeDirection" : true, "width" : 150 * mm, "height" : 150 * mm});
        }
        {
            var Q0;
            Q0=qCreatedBy(id+"F53.planeOp",FACE);
            var sketch = newSketch(context, id + "F54", { "sketchPlane" : qUnion([Q0])});
            skLineSegment(sketch, "E45.bottom", {"start": v(495.97, 860) * mm, "end": v(-64.03, 860) * mm});
            skLineSegment(sketch, "E45.top", {"start": v(495.97, 200) * mm, "end": v(-64.03, 200) * mm});
            skLineSegment(sketch, "E45.left", {"start": v(495.97, 860) * mm, "end": v(495.97, 200) * mm});
            skLineSegment(sketch, "E45.right", {"start": v(-64.03, 860) * mm, "end": v(-64.03, 200) * mm});
            skSolve(sketch);
        }
        {
            var Q0;
            Q0 = qSketchRegion(id + "F54", true);
            extrude(context, id + "F55", {"entities" : qUnion([Q0]), "operationType" : NewBodyOperationType.REMOVE, "oppositeDirection" : true, "depth" : 580 * mm, "offsetDistance" : 25 * mm});
        }
        {
            var Q0;
            Q0=makeQuery(id+"F28.boolean.opBoolean","MERGE",FACE,{"derivedFrom":[makeQuery(id+"F27.boolean.opBoolean","MERGE",FACE,{"derivedFrom":[makeQuery(id+"F24.opExtrude","SWEPT_FACE",FACE,{"disambiguationData":[OSD([sQuery(id+"F23.wireOp",EDGE,"E19.top")])]}),makeQuery(id+"F27.opExtrude","SWEPT_FACE",FACE,{"disambiguationData":[OSD([sQuery(id+"F22.wireOp",EDGE,"E18.top")])]})]}),makeQuery(id+"F28.opExtrude","SWEPT_FACE",FACE,{"disambiguationData":[OSD([sQuery(id+"F21.wireOp",EDGE,"E17.top")])]})]});
            var sketch = newSketch(context, id + "F56", { "sketchPlane" : qUnion([Q0])});
            skLineSegment(sketch, "E46.bottom", {"start": v(-84.03, 2080) * mm, "end": v(-684.03, 2080) * mm});
            skLineSegment(sketch, "E46.top", {"start": v(-84.03, 1480) * mm, "end": v(-684.03, 1480) * mm});
            skLineSegment(sketch, "E46.left", {"start": v(-84.03, 2080) * mm, "end": v(-84.03, 1480) * mm});
            skLineSegment(sketch, "E46.right", {"start": v(-684.03, 2080) * mm, "end": v(-684.03, 1480) * mm});
            skLineSegment(sketch, "E47.0", {"start": v(-104.03, 2060) * mm, "end": v(-664.03, 2060) * mm});
            skLineSegment(sketch, "E47.1", {"start": v(-104.03, 2060) * mm, "end": v(-104.03, 1500) * mm});
            skLineSegment(sketch, "E47.2", {"start": v(-104.03, 1500) * mm, "end": v(-664.03, 1500) * mm});
            skLineSegment(sketch, "E47.3", {"start": v(-664.03, 2060) * mm, "end": v(-664.03, 1500) * mm});
            skSolve(sketch);
        }
        {
            var Q0;
            Q0=makeQuery(id+"F56.imprint","IMPRINT",FACE,{"disambiguationData":[TD([[makeQuery(id+"F56.imprint","IMPRINT",EDGE,{"derivedFrom":sQuery(id+"F56.wireOp",EDGE,"E47.0")}),1.0]])]});
            var sketch = newSketch(context, id + "F57", { "sketchPlane" : qUnion([Q0])});
            skLineSegment(sketch, "E48.bottom", {"start": v(-104.03, 1790) * mm, "end": v(-664.03, 1790) * mm});
            skLineSegment(sketch, "E48.top", {"start": v(-104.03, 1770) * mm, "end": v(-664.03, 1770) * mm});
            skSolve(sketch);
        }
        {
            var Q0;
            {var subQ0=sQuery(id+"F57.wireOp",EDGE,"E48.bottom");Q0=makeQuery(id+"F57.imprint","IMPRINT",FACE,{"disambiguationData":[TD([[makeQuery(id+"F57.imprint","IMPRINT",EDGE,{"derivedFrom":subQ0}),-1.0]])]});}
            extrude(context, id + "F58", {"entities" : qUnion([Q0]), "operationType" : NewBodyOperationType.REMOVE, "oppositeDirection" : true, "depth" : 350 * mm, "offsetDistance" : 25 * mm});
        }
        {
            var Q0;
            {var subQ0=sQuery(id+"F57.wireOp",EDGE,"E48.top");Q0=makeQuery(id+"F57.imprint","IMPRINT",FACE,{"disambiguationData":[TD([[makeQuery(id+"F57.imprint","IMPRINT",EDGE,{"derivedFrom":subQ0}),1.0]])]});}
            extrude(context, id + "F59", {"entities" : qUnion([Q0]), "operationType" : NewBodyOperationType.REMOVE, "oppositeDirection" : true, "depth" : 350 * mm, "offsetDistance" : 25 * mm});
        }
        {
            var Q0;
            Q0=makeQuery(id+"F28.boolean.opBoolean","MERGE",FACE,{"derivedFrom":[makeQuery(id+"F27.boolean.opBoolean","MERGE",FACE,{"derivedFrom":[makeQuery(id+"F24.opExtrude","SWEPT_FACE",FACE,{"disambiguationData":[OSD([sQuery(id+"F23.wireOp",EDGE,"E19.top")])]}),makeQuery(id+"F27.opExtrude","SWEPT_FACE",FACE,{"disambiguationData":[OSD([sQuery(id+"F22.wireOp",EDGE,"E18.top")])]})]}),makeQuery(id+"F28.opExtrude","SWEPT_FACE",FACE,{"disambiguationData":[OSD([sQuery(id+"F21.wireOp",EDGE,"E17.top")])]})]});
            var sketch = newSketch(context, id + "F60", { "sketchPlane" : qUnion([Q0])});
            skLineSegment(sketch, "E49.bottom", {"start": v(-84.03, 2080) * mm, "end": v(-684.03, 2080) * mm});
            skLineSegment(sketch, "E49.top", {"start": v(-84.03, 1480) * mm, "end": v(-684.03, 1480) * mm});
            skLineSegment(sketch, "E49.left", {"start": v(-84.03, 2080) * mm, "end": v(-84.03, 1480) * mm});
            skLineSegment(sketch, "E49.right", {"start": v(-684.03, 2080) * mm, "end": v(-684.03, 1480) * mm});
            skSolve(sketch);
        }
        {
            var Q0;
            Q0 = qSketchRegion(id + "F60", true);
            extrude(context, id + "F61", {"entities" : qUnion([Q0]), "operationType" : NewBodyOperationType.ADD, "depth" : 25 * mm, "offsetDistance" : 25 * mm});
        }
        {
            var Q0;
            Q0=qCreatedBy(id+"F6.planeOp",FACE);
            var sketch = newSketch(context, id + "F62", { "sketchPlane" : qUnion([Q0])});
            skLineSegment(sketch, "E50.bottom", {"start": v(1352.93, -2045.62) * mm, "end": v(552.93, -2045.62) * mm});
            skLineSegment(sketch, "E50.top", {"start": v(1352.93, -2645.62) * mm, "end": v(552.93, -2645.62) * mm});
            skLineSegment(sketch, "E50.left", {"start": v(1352.93, -2045.62) * mm, "end": v(1352.93, -2645.62) * mm});
            skLineSegment(sketch, "E50.right", {"start": v(552.93, -2045.62) * mm, "end": v(552.93, -2645.62) * mm});
            skSolve(sketch);
        }
        {
            var Q0;
            Q0=qCreatedBy(id+"F6.planeOp",FACE);
            var sketch = newSketch(context, id + "F63", { "sketchPlane" : qUnion([Q0])});
            skLineSegment(sketch, "E51.bottom", {"start": v(552.93, -2045.62) * mm, "end": v(-247.07, -2045.62) * mm});
            skLineSegment(sketch, "E51.top", {"start": v(552.93, -2645.62) * mm, "end": v(-247.07, -2645.62) * mm});
            skLineSegment(sketch, "E51.left", {"start": v(552.93, -2045.62) * mm, "end": v(552.93, -2645.62) * mm});
            skLineSegment(sketch, "E51.right", {"start": v(-247.07, -2045.62) * mm, "end": v(-247.07, -2645.62) * mm});
            skSolve(sketch);
        }
        {
            var Q0;
            Q0=makeQuery(id+"F0.imprint","IMPRINT",FACE,{"disambiguationData":[TD([[makeQuery(id+"F0.imprint","IMPRINT",EDGE,{"derivedFrom":sQuery(id+"F0.wireOp",EDGE,"E0")}),1.0]])]});
            extrude(context, id + "F64", {"entities" : qUnion([Q0]), "operationType" : NewBodyOperationType.ADD, "depth" : 80 * mm, "offsetDistance" : 25 * mm});
        }
        {
            var Q0;
            Q0 = qSketchRegion(id + "F62", true);
            extrude(context, id + "F65", {"entities" : qUnion([Q0]), "operationType" : NewBodyOperationType.ADD, "depth" : 800 * mm, "offsetDistance" : 25 * mm});
        }
        {
            var Q0;
            Q0 = qSketchRegion(id + "F63", true);
            extrude(context, id + "F66", {"entities" : qUnion([Q0]), "operationType" : NewBodyOperationType.ADD, "depth" : 800 * mm, "offsetDistance" : 25 * mm});
        }
        {
            var Q0;
            Q0=makeQuery(id+"F66.boolean.opBoolean","MERGE",FACE,{"derivedFrom":[makeQuery(id+"F65.opExtrude","SWEPT_FACE",FACE,{"disambiguationData":[OSD([sQuery(id+"F62.wireOp",EDGE,"E50.top")])]}),makeQuery(id+"F66.opExtrude","SWEPT_FACE",FACE,{"disambiguationData":[OSD([sQuery(id+"F63.wireOp",EDGE,"E51.top")])]})]});
            cPlane(context, id + "F67", {"entities" : qUnion([Q0]), "cplaneType" : CPlaneType.OFFSET, "offset" : 5 * mm, "width" : 150 * mm, "height" : 150 * mm});
        }
        {
            var Q0;
            Q0=qCreatedBy(id+"F67.planeOp",FACE);
            var sketch = newSketch(context, id + "F68", { "sketchPlane" : qUnion([Q0])});
            skLineSegment(sketch, "E52.bottom", {"start": v(1352.93, 880) * mm, "end": v(-247.07, 880) * mm});
            skLineSegment(sketch, "E52.top", {"start": v(1352.93, 80) * mm, "end": v(-247.07, 80) * mm});
            skLineSegment(sketch, "E52.left", {"start": v(1352.93, 880) * mm, "end": v(1352.93, 80) * mm});
            skLineSegment(sketch, "E52.right", {"start": v(-247.07, 880) * mm, "end": v(-247.07, 80) * mm});
            skSolve(sketch);
        }
        {
            var Q0;
            Q0 = qSketchRegion(id + "F68", true);
            extrude(context, id + "F69", {"entities" : qUnion([Q0]), "depth" : 25 * mm, "offsetDistance" : 25 * mm});
        }
        {
            var Q0;
            Q0 = qSketchRegion(id + "F68", true);
            extrude(context, id + "F70", {"entities" : qUnion([Q0]), "operationType" : NewBodyOperationType.ADD, "depth" : 20 * mm, "offsetDistance" : 25 * mm});
        }
        {
            var Q0;
            Q0=makeQuery(id+"F69.opExtrude","CAP_FACE",FACE,{"disambiguationData":[OSD([sQuery(id+"F68.wireOp",EDGE,"E52.bottom"),sQuery(id+"F68.wireOp",EDGE,"E52.top"),sQuery(id+"F68.wireOp",EDGE,"E52.left"),sQuery(id+"F68.wireOp",EDGE,"E52.right")])],"isStart":false});
            var sketch = newSketch(context, id + "F71", { "sketchPlane" : qUnion([Q0])});
            skLineSegment(sketch, "E53.bottom", {"start": v(-247.07, 880) * mm, "end": v(552.93, 880) * mm});
            skLineSegment(sketch, "E53.top", {"start": v(-247.07, 480) * mm, "end": v(552.93, 480) * mm});
            skLineSegment(sketch, "E53.left", {"start": v(-247.07, 880) * mm, "end": v(-247.07, 480) * mm});
            skLineSegment(sketch, "E53.right", {"start": v(552.93, 880) * mm, "end": v(552.93, 480) * mm});
            skLineSegment(sketch, "E54.0", {"start": v(-244.57, 877.5) * mm, "end": v(550.43, 877.5) * mm});
            skLineSegment(sketch, "E54.1", {"start": v(-244.57, 877.5) * mm, "end": v(-244.57, 482.5) * mm});
            skLineSegment(sketch, "E54.2", {"start": v(-244.57, 482.5) * mm, "end": v(550.43, 482.5) * mm});
            skLineSegment(sketch, "E54.3", {"start": v(550.43, 877.5) * mm, "end": v(550.43, 482.5) * mm});
            skSolve(sketch);
        }
        {
            var Q0;
            Q0=makeQuery(id+"F71.imprint","IMPRINT",FACE,{"disambiguationData":[TD([[makeQuery(id+"F71.imprint","IMPRINT",EDGE,{"derivedFrom":sQuery(id+"F71.wireOp",EDGE,"E53.bottom")}),1.0]])]});
            extrude(context, id + "F72", {"entities" : qUnion([Q0]), "operationType" : NewBodyOperationType.REMOVE, "oppositeDirection" : true, "depth" : 25 * mm, "offsetDistance" : 25 * mm});
        }
        {
            var Q0;
            {var subQ0=sQuery(id+"F68.wireOp",EDGE,"E52.left");var subQ1=sQuery(id+"F68.wireOp",EDGE,"E52.top");var subQ2=sQuery(id+"F68.wireOp",EDGE,"E52.right");var subQ3=sQuery(id+"F68.wireOp",EDGE,"E52.bottom");Q0=makeQuery(id+"F72.boolean.opBoolean","SPLIT",FACE,{"disambiguationData":[TD([makeQuery(id+"F69.opExtrude","SWEPT_FACE",FACE,{"disambiguationData":[OSD([subQ3])]})])],"derivedFrom":makeQuery(id+"F69.opExtrude","CAP_FACE",FACE,{"disambiguationData":[OSD([subQ3,subQ1,subQ0,subQ2])],"isStart":false})});}
            var sketch = newSketch(context, id + "F73", { "sketchPlane" : qUnion([Q0])});
            skLineSegment(sketch, "E55.bottom", {"start": v(-247.07, 480) * mm, "end": v(552.93, 480) * mm});
            skLineSegment(sketch, "E55.top", {"start": v(-247.07, 80) * mm, "end": v(552.93, 80) * mm});
            skLineSegment(sketch, "E55.left", {"start": v(-247.07, 480) * mm, "end": v(-247.07, 80) * mm});
            skLineSegment(sketch, "E55.right", {"start": v(552.93, 480) * mm, "end": v(552.93, 80) * mm});
            skLineSegment(sketch, "E56.0", {"start": v(550.43, 480) * mm, "end": v(550.43, 82.5) * mm});
            skLineSegment(sketch, "E56.1", {"start": v(-244.57, 82.5) * mm, "end": v(550.43, 82.5) * mm});
            skLineSegment(sketch, "E56.2", {"start": v(-244.57, 480) * mm, "end": v(-244.57, 82.5) * mm});
            skSolve(sketch);
        }
        {
            var Q0;
            Q0=makeQuery(id+"F73.imprint","IMPRINT",FACE,{"disambiguationData":[TD([[makeQuery(id+"F73.imprint","IMPRINT",EDGE,{"derivedFrom":sQuery(id+"F73.wireOp",EDGE,"E55.top")}),-1.0]])]});
            extrude(context, id + "F74", {"entities" : qUnion([Q0]), "operationType" : NewBodyOperationType.REMOVE, "oppositeDirection" : true, "depth" : 25 * mm, "offsetDistance" : 25 * mm});
        }
        {
            var Q0;
            {var subQ1=sQuery(id+"F68.wireOp",EDGE,"E52.bottom");var subQ2=makeQuery(id+"F69.opExtrude","SWEPT_FACE",FACE,{"disambiguationData":[OSD([subQ1])]});var subQ3=sQuery(id+"F68.wireOp",EDGE,"E52.left");var subQ5=sQuery(id+"F68.wireOp",EDGE,"E52.top");var subQ7=sQuery(id+"F68.wireOp",EDGE,"E52.right");Q0=makeQuery(id+"F74.boolean.opBoolean","SPLIT",FACE,{"disambiguationData":[TD([subQ2])],"derivedFrom":makeQuery(id+"F72.boolean.opBoolean","SPLIT",FACE,{"disambiguationData":[TD([subQ2])],"derivedFrom":makeQuery(id+"F69.opExtrude","CAP_FACE",FACE,{"disambiguationData":[OSD([subQ1,subQ5,subQ3,subQ7])],"isStart":false})})});}
            var sketch = newSketch(context, id + "F75", { "sketchPlane" : qUnion([Q0])});
            skLineSegment(sketch, "E57.bottom", {"start": v(1352.93, 880) * mm, "end": v(552.93, 880) * mm});
            skLineSegment(sketch, "E57.top", {"start": v(1352.93, 480) * mm, "end": v(552.93, 480) * mm});
            skLineSegment(sketch, "E57.left", {"start": v(1352.93, 880) * mm, "end": v(1352.93, 480) * mm});
            skLineSegment(sketch, "E57.right", {"start": v(552.93, 880) * mm, "end": v(552.93, 480) * mm});
            skLineSegment(sketch, "E58.0", {"start": v(1350.43, 877.5) * mm, "end": v(555.43, 877.5) * mm});
            skLineSegment(sketch, "E58.1", {"start": v(1350.43, 877.5) * mm, "end": v(1350.43, 482.5) * mm});
            skLineSegment(sketch, "E58.2", {"start": v(1350.43, 482.5) * mm, "end": v(555.43, 482.5) * mm});
            skLineSegment(sketch, "E58.3", {"start": v(555.43, 877.5) * mm, "end": v(555.43, 482.5) * mm});
            skSolve(sketch);
        }
        {
            var Q0;
            Q0=makeQuery(id+"F75.imprint","IMPRINT",FACE,{"disambiguationData":[TD([[makeQuery(id+"F75.imprint","IMPRINT",EDGE,{"derivedFrom":sQuery(id+"F75.wireOp",EDGE,"E57.bottom")}),1.0]])]});
            extrude(context, id + "F76", {"entities" : qUnion([Q0]), "operationType" : NewBodyOperationType.REMOVE, "oppositeDirection" : true, "depth" : 25 * mm, "offsetDistance" : 25 * mm});
        }
        {
            var Q0;
            {var subQ0=sQuery(id+"F68.wireOp",EDGE,"E52.top");var subQ1=makeQuery(id+"F69.opExtrude","SWEPT_FACE",FACE,{"disambiguationData":[OSD([subQ0])]});var subQ2=sQuery(id+"F68.wireOp",EDGE,"E52.left");var subQ6=sQuery(id+"F68.wireOp",EDGE,"E52.bottom");var subQ7=makeQuery(id+"F69.opExtrude","SWEPT_FACE",FACE,{"disambiguationData":[OSD([subQ6])]});var subQ8=sQuery(id+"F68.wireOp",EDGE,"E52.right");Q0=makeQuery(id+"F76.boolean.opBoolean","SPLIT",FACE,{"disambiguationData":[TD([subQ1])],"derivedFrom":makeQuery(id+"F74.boolean.opBoolean","SPLIT",FACE,{"disambiguationData":[TD([subQ7])],"derivedFrom":makeQuery(id+"F72.boolean.opBoolean","SPLIT",FACE,{"disambiguationData":[TD([subQ7])],"derivedFrom":makeQuery(id+"F69.opExtrude","CAP_FACE",FACE,{"disambiguationData":[OSD([subQ6,subQ0,subQ2,subQ8])],"isStart":false})})})});}
            var sketch = newSketch(context, id + "F77", { "sketchPlane" : qUnion([Q0])});
            skLineSegment(sketch, "E59.bottom", {"start": v(552.93, 480) * mm, "end": v(1352.93, 480) * mm});
            skLineSegment(sketch, "E59.top", {"start": v(552.93, 80) * mm, "end": v(1352.93, 80) * mm});
            skLineSegment(sketch, "E59.left", {"start": v(552.93, 480) * mm, "end": v(552.93, 80) * mm});
            skLineSegment(sketch, "E59.right", {"start": v(1352.93, 480) * mm, "end": v(1352.93, 80) * mm});
            skLineSegment(sketch, "E60.0", {"start": v(555.43, 477.5) * mm, "end": v(1350.43, 477.5) * mm});
            skLineSegment(sketch, "E60.1", {"start": v(555.43, 477.5) * mm, "end": v(555.43, 82.5) * mm});
            skLineSegment(sketch, "E60.2", {"start": v(555.43, 82.5) * mm, "end": v(1350.43, 82.5) * mm});
            skLineSegment(sketch, "E60.3", {"start": v(1350.43, 477.5) * mm, "end": v(1350.43, 82.5) * mm});
            skSolve(sketch);
        }
        {
            var Q0;
            Q0=makeQuery(id+"F77.imprint","IMPRINT",FACE,{"disambiguationData":[TD([[makeQuery(id+"F77.imprint","IMPRINT",EDGE,{"derivedFrom":sQuery(id+"F77.wireOp",EDGE,"E59.bottom")}),1.0]])]});
            extrude(context, id + "F78", {"entities" : qUnion([Q0]), "operationType" : NewBodyOperationType.REMOVE, "oppositeDirection" : true, "depth" : 25 * mm, "offsetDistance" : 25 * mm});
        }
        {
            var Q0;
            Q0=makeQuery(id+"F66.boolean.opBoolean","MERGE",FACE,{"derivedFrom":[makeQuery(id+"F65.opExtrude","CAP_FACE",FACE,{"disambiguationData":[OSD([sQuery(id+"F62.wireOp",EDGE,"E50.bottom"),sQuery(id+"F62.wireOp",EDGE,"E50.top"),sQuery(id+"F62.wireOp",EDGE,"E50.left"),sQuery(id+"F62.wireOp",EDGE,"E50.right")])],"isStart":false}),makeQuery(id+"F66.opExtrude","CAP_FACE",FACE,{"disambiguationData":[OSD([sQuery(id+"F63.wireOp",EDGE,"E51.bottom"),sQuery(id+"F63.wireOp",EDGE,"E51.top"),sQuery(id+"F63.wireOp",EDGE,"E51.left"),sQuery(id+"F63.wireOp",EDGE,"E51.right")])],"isStart":false})]});
            cPlane(context, id + "F79", {"entities" : qUnion([Q0]), "cplaneType" : CPlaneType.OFFSET, "offset" : 0 * mm, "width" : 150 * mm, "height" : 150 * mm});
        }
        {
            var Q0;
            Q0=makeQuery(id+"F26.boolean.opBoolean","MERGE",FACE,{"derivedFrom":[makeQuery(id+"F18.boolean.opBoolean","MERGE",FACE,{"derivedFrom":[makeQuery(id+"F17.boolean.opBoolean","MERGE",FACE,{"derivedFrom":[makeQuery(id+"F16.boolean.opBoolean","MERGE",FACE,{"derivedFrom":[makeQuery(id+"F15.boolean.opBoolean","MERGE",FACE,{"derivedFrom":[makeQuery(id+"F14.opExtrude","CAP_FACE",FACE,{"disambiguationData":[OSD([sQuery(id+"F8.wireOp",EDGE,"E10.bottom"),sQuery(id+"F8.wireOp",EDGE,"E10.top"),sQuery(id+"F8.wireOp",EDGE,"E10.left"),sQuery(id+"F8.wireOp",EDGE,"E10.right")])],"isStart":false}),makeQuery(id+"F15.opExtrude","CAP_FACE",FACE,{"disambiguationData":[OSD([sQuery(id+"F9.wireOp",EDGE,"E11.bottom"),sQuery(id+"F9.wireOp",EDGE,"E11.top"),sQuery(id+"F9.wireOp",EDGE,"E11.left"),sQuery(id+"F9.wireOp",EDGE,"E11.right")])],"isStart":false})]}),makeQuery(id+"F16.opExtrude","CAP_FACE",FACE,{"disambiguationData":[OSD([sQuery(id+"F10.wireOp",EDGE,"E12.bottom"),sQuery(id+"F10.wireOp",EDGE,"E12.top"),sQuery(id+"F10.wireOp",EDGE,"E12.left"),sQuery(id+"F10.wireOp",EDGE,"E12.right")])],"isStart":false})]}),makeQuery(id+"F17.opExtrude","CAP_FACE",FACE,{"disambiguationData":[OSD([sQuery(id+"F11.wireOp",EDGE,"E13.bottom"),sQuery(id+"F11.wireOp",EDGE,"E13.top"),sQuery(id+"F11.wireOp",EDGE,"E13.left"),sQuery(id+"F11.wireOp",EDGE,"E13.right")])],"isStart":false})]}),makeQuery(id+"F18.opExtrude","CAP_FACE",FACE,{"disambiguationData":[OSD([sQuery(id+"F12.wireOp",EDGE,"E14.bottom"),sQuery(id+"F12.wireOp",EDGE,"E14.top"),sQuery(id+"F12.wireOp",EDGE,"E14.left"),sQuery(id+"F12.wireOp",EDGE,"E14.right")])],"isStart":false})]})],"fromTools":[makeQuery(id+"F26.opExtrude","SWEPT_FACE",FACE,{"disambiguationData":[OSD([sQuery(id+"F25.wireOp",EDGE,"E20.bottom")])]})]});
            var sketch = newSketch(context, id + "F80", { "sketchPlane" : qUnion([Q0])});
            skLineSegment(sketch, "E61.bottom", {"start": v(1115.97, -225.48) * mm, "end": v(-1684.03, -225.48) * mm});
            skLineSegment(sketch, "E61.top", {"start": v(1115.97, -855.48) * mm, "end": v(-1684.03, -855.48) * mm});
            skLineSegment(sketch, "E61.left", {"start": v(1115.97, -225.48) * mm, "end": v(1115.97, -855.48) * mm});
            skLineSegment(sketch, "E61.right", {"start": v(-1684.03, -225.48) * mm, "end": v(-1684.03, -855.48) * mm});
            skSolve(sketch);
        }
        {
            var Q0;
            {var subQ0=sQuery(id+"F80.wireOp",EDGE,"E61.bottom");Q0=makeQuery(id+"F80.imprint","IMPRINT",FACE,{"disambiguationData":[TD([[makeQuery(id+"F80.imprint","IMPRINT",EDGE,{"derivedFrom":subQ0}),1.0]])]});}
            var sketch = newSketch(context, id + "F81", { "sketchPlane" : qUnion([Q0])});
            skLineSegment(sketch, "E62.bottom", {"start": v(1352.93, -2045.62) * mm, "end": v(-247.07, -2045.62) * mm});
            skLineSegment(sketch, "E62.top", {"start": v(1352.93, -2675.62) * mm, "end": v(-247.07, -2675.62) * mm});
            skLineSegment(sketch, "E62.left", {"start": v(1352.93, -2045.62) * mm, "end": v(1352.93, -2675.62) * mm});
            skLineSegment(sketch, "E62.right", {"start": v(-247.07, -2045.62) * mm, "end": v(-247.07, -2675.62) * mm});
            skSolve(sketch);
        }
        {
            var Q0;
            Q0 = qSketchRegion(id + "F80", true);
            extrude(context, id + "F82", {"entities" : qUnion([Q0]), "depth" : 40 * mm, "offsetDistance" : 25 * mm});
        }
        {
            var Q0;
            Q0 = qSketchRegion(id + "F81", true);
            extrude(context, id + "F83", {"entities" : qUnion([Q0]), "depth" : 40 * mm, "offsetDistance" : 25 * mm});
        }
        {
            var Q0;
            Q0=qCreatedBy(id+"F79.planeOp",FACE);
            cPlane(context, id + "F84", {"entities" : qUnion([Q0]), "cplaneType" : CPlaneType.OFFSET, "offset" : 150 * mm, "oppositeDirection" : true, "width" : 150 * mm, "height" : 150 * mm});
        }
        {
            var Q0;
            Q0=qCreatedBy(id+"F84.planeOp",FACE);
            var sketch = newSketch(context, id + "F85", { "sketchPlane" : qUnion([Q0])});
            skLineSegment(sketch, "E63", {"start": v(1352.93, -2045.62) * mm, "end": v(1352.93, -1620.62) * mm});
            skLineSegment(sketch, "E64", {"start": v(-1247.07, -1620.62) * mm, "end": v(-1247.07, -2525.62) * mm});
            skLineSegment(sketch, "E65", {"start": v(-1172.07, -2675.62) * mm, "end": v(-247.07, -2675.62) * mm});
            skLineSegment(sketch, "E66", {"start": v(-247.07, -2675.62) * mm, "end": v(-247.07, -2045.62) * mm});
            skLineSegment(sketch, "E67", {"start": v(-247.07, -2045.62) * mm, "end": v(1352.93, -2045.62) * mm});
            skLineSegment(sketch, "E68.top", {"start": v(-1172.07, -1545.62) * mm, "end": v(-1097.07, -1545.62) * mm});
            skLineSegment(sketch, "E68.left", {"start": v(-1247.07, -1695.62) * mm, "end": v(-1247.07, -1620.62) * mm});
            skPoint(sketch, "E68.middle", {"position": v(-1172.07, -1620.62) * mm});
            skLineSegment(sketch, "E69.bottom", {"start": v(-1172.07, -2675.62) * mm, "end": v(-1097.07, -2675.62) * mm});
            skLineSegment(sketch, "E69.left", {"start": v(-1247.07, -2600.62) * mm, "end": v(-1247.07, -2525.62) * mm});
            skPoint(sketch, "E69.middle", {"position": v(-1172.07, -2600.62) * mm});
            skArc(sketch, "E70", {"start": v(-1247.07, -2600.62) * mm, "mid": v(-1225.1, -2653.65) * mm, "end": v(-1172.07, -2675.62) * mm});
            skArc(sketch, "E71", {"start": v(-1172.07, -1545.62) * mm, "mid": v(-1225.1, -1567.59) * mm, "end": v(-1247.07, -1620.62) * mm});
            skPoint(sketch, "E68.right.start.orphan", {"position": v(-1097.07, -1695.62) * mm});
            skPoint(sketch, "E72.orphan", {"position": v(-1247.07, -1545.62) * mm});
            skPoint(sketch, "E73.orphan", {"position": v(-1247.07, -2675.62) * mm});
            skPoint(sketch, "E69.right.end.orphan", {"position": v(-1097.07, -2525.62) * mm});
            skPoint(sketch, "E74.middle", {"position": v(1444.76, -1453.8) * mm});
            skPoint(sketch, "E75.orphan", {"position": v(1536.59, -1361.97) * mm});
            skPoint(sketch, "E76.orphan", {"position": v(1352.93, -1545.62) * mm});
            skLineSegment(sketch, "E77.trimOffspring", {"start": v(1277.93, -1545.62) * mm, "end": v(-1172.07, -1545.62) * mm});
            skPoint(sketch, "E74.top.start.orphan", {"position": v(1536.59, -1545.62) * mm});
            skPoint(sketch, "E74.right.start.orphan", {"position": v(1352.93, -1361.97) * mm});
            skLineSegment(sketch, "E78.top", {"start": v(1202.93, -1545.62) * mm, "end": v(1277.93, -1545.62) * mm});
            skLineSegment(sketch, "E78.right", {"start": v(1352.93, -1695.62) * mm, "end": v(1352.93, -1620.62) * mm});
            skPoint(sketch, "E78.middle", {"position": v(1277.93, -1620.62) * mm});
            skArc(sketch, "E79", {"start": v(1352.93, -1620.62) * mm, "mid": v(1330.97, -1567.59) * mm, "end": v(1277.93, -1545.62) * mm});
            skPoint(sketch, "E80.orphan", {"position": v(1202.93, -1695.62) * mm});
            skSolve(sketch);
        }
        {
            var Q0;
            Q0=makeQuery(id+"F85.imprint","IMPRINT",FACE,{"disambiguationData":[TD([[makeQuery(id+"F85.imprint","IMPRINT",EDGE,{"derivedFrom":sQuery(id+"F85.wireOp",EDGE,"E63")}),1.0]])]});
            extrude(context, id + "F86", {"entities" : qUnion([Q0]), "oppositeDirection" : true, "depth" : 40 * mm, "offsetDistance" : 25 * mm});
        }
    });
